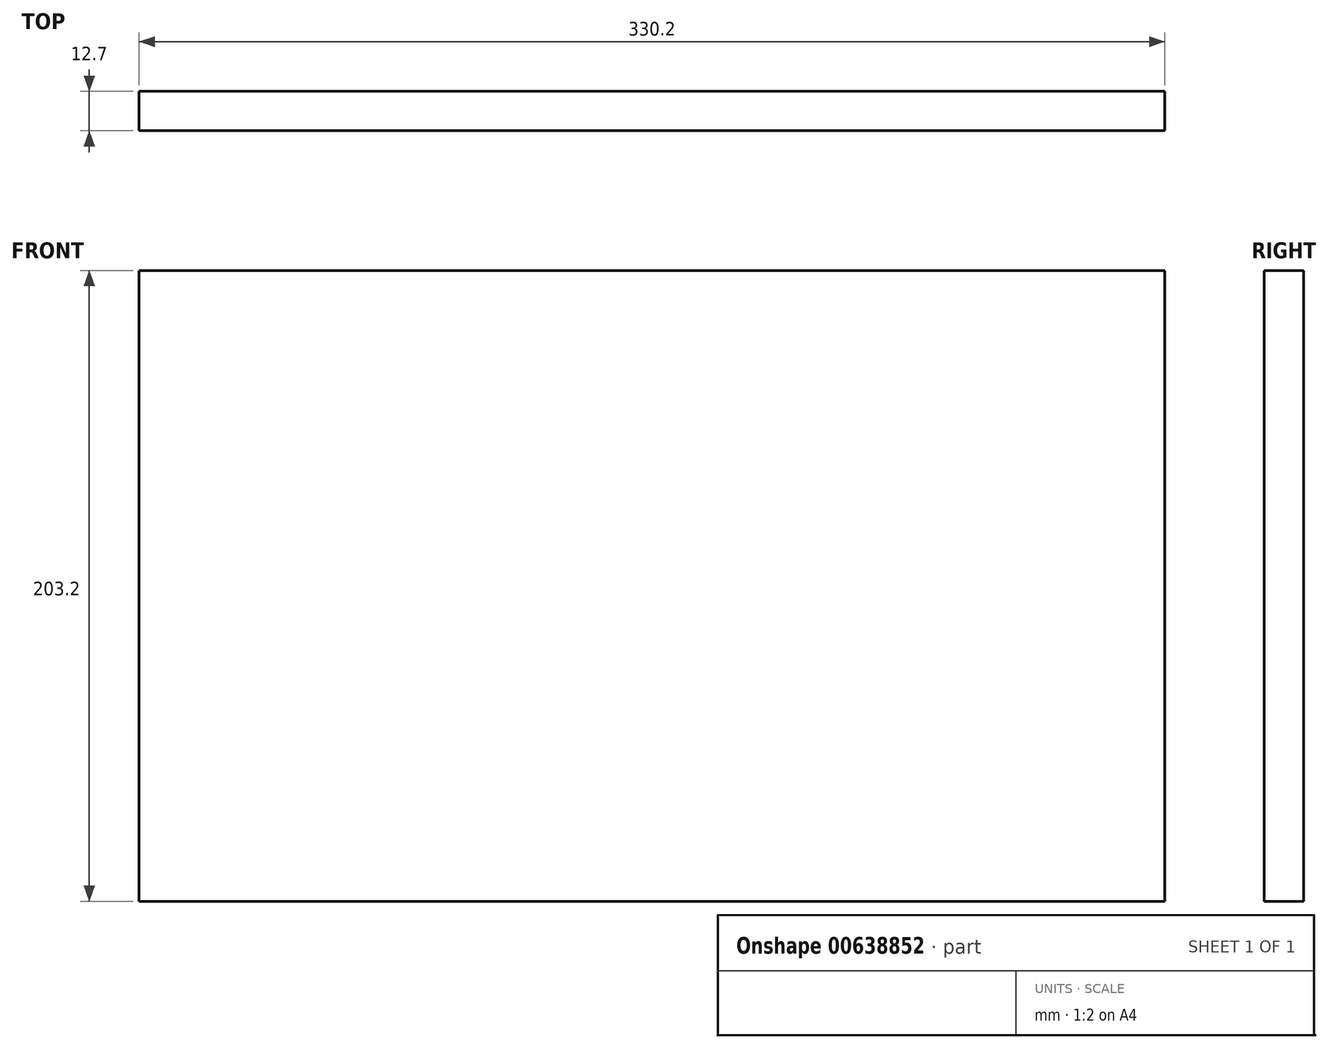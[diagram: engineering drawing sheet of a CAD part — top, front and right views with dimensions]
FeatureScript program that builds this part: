
annotation { "Feature Type Name" : "Feature", "Feature Type Description" : "" }
export const myFeature = defineFeature(function(context is Context, id is Id, definition is map)
    precondition{}
    {
        {
            var Q0;
            Q0=qCreatedBy(makeId("Front.planeOp"),FACE);
            var sketch = newSketch(context, id + "F0", { "sketchPlane" : qUnion([Q0])});
            skLineSegment(sketch, "E0.bottom", {"start": v(165.1, 101.6) * mm, "end": v(-165.1, 101.6) * mm});
            skLineSegment(sketch, "E0.top", {"start": v(165.1, -101.6) * mm, "end": v(-165.1, -101.6) * mm});
            skLineSegment(sketch, "E0.left", {"start": v(165.1, 101.6) * mm, "end": v(165.1, -101.6) * mm});
            skLineSegment(sketch, "E0.right", {"start": v(-165.1, 101.6) * mm, "end": v(-165.1, -101.6) * mm});
            skPoint(sketch, "E0.middle", {"position": v(0, 0) * mm});
            skSolve(sketch);
        }
        {
            var Q0;
            Q0=makeQuery(id+"F0.imprint","IMPRINT",FACE,{"disambiguationData":[TD([[makeQuery(id+"F0.imprint","IMPRINT",EDGE,{"derivedFrom":sQuery(id+"F0.wireOp",EDGE,"E0.bottom")}),1.0]])]});
            extrude(context, id + "F1", {"entities" : qUnion([Q0]), "depth" : 12.7 * mm, "offsetDistance" : 25.4 * mm});
        }
    });
